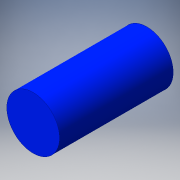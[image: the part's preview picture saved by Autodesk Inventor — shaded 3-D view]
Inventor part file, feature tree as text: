
AUTODESK INVENTOR PART (.ipt)
format: ipt  version: 2016 SP1 (Build 200210100, 210)  size: 94,208 bytes
history: native  units: in
note: dims shown in document units (in); Inventor stores cm internally (conversion verified against a paired STEP export)
features: extrude x1, sketch x1
ambient origin geometry x8: Origin, YZ Plane, XZ Plane, XY Plane, X Axis, Y Axis, Z Axis, Center Point
bodies: Solid1 (feature_tree)
feature tree (2):
  extrude  "Extrusion1"  Depth=2.125in TaperAngle=0.0deg
  sketch  "Sketch1"  dims[d0=0.9843in d1=2.125in d2=0.0in]
